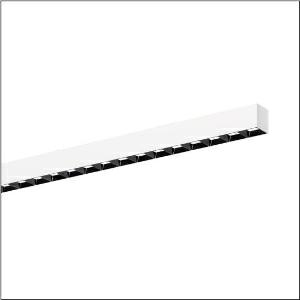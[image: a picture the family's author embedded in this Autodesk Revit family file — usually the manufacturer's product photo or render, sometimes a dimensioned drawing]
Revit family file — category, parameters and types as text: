
# Revit family: silica_r__21_51mx22dc4awb_3425
name_source: partatom
category: Lighting Fixtures
units: mm (PartAtom-declared; Revit-internal decimal feet)

## family parameters
Cut with Voids When Loaded = No
Host = Face
Light Source = No
Part Type = Normal
Room Calculation Point = No
Round Connector Dimension = Use Diameter
Shared = No

## types (1)
- --- (1 x LED, 10800 lm, 64.7 W, 4000K)
    Apparent Load = 65 VA
    CIE Flux Codes = 86 100 100 100 100
    Color Rendering = 80
    Color Temperature = 4000K
    Default Elevation = 1800 mm
    Description = Silica® 21, office luminaire, primary light control with darklight reflector, of PMMA, black, CAT 2 (L<= 3000cd/m²), light emission: direct distribution, primary light characteristic: symmetric, installation type: surface-mounted, LED, rated luminous flux: 10.800lm, luminous efficacy: 167lm/W, light colour: 840, colour temperature: 4000K, with terminal, 3+2-pole, max. 2.5mm², mains connection: 220..240V, AC, 50/60Hz, rated input power: 64.7W, luminaire housing, of aluminium, traffic white (RAL 9016), length: 3.004mm, width: 53mm, height: 53mm, protection rating (complete): IP20, insulation class (complete): insulation class I (protective earthing), certification: CE, permissible operating ambient temperature: 0..+35°C, standard: EN 50419, packaging unit: 1 piece
    Height = 0 mm  [stored 0 ft]
    Lamp = 1 x LED
    Lamp Light Flux = 10800 lm
    Lamp Power = 64.7 W
    Lamp count = 1
    Length = 3004 mm
    Luminous efficacy = 167 lm/W
    Manufacturer = Siteco
    ModVariant = No
    Model = 51MX22DC4AWB
    Mounting Place = Ceiling
    Mounting Type = Recessed
    Number of Poles = 1
    OnlyDefault = Yes
    Power Factor = 1
    Product Name = Silica® 21
    Product group = office luminaire | ceiling recessed
    ProductGroupID = 400
    Protection Class = Protection class I
    Protection Degree = IP 20
    RLX_Detail_Level = 1
    RLX_Emergency_Light_Flux = 0 lm
    RLX_Emergency_Type = 0
    RLX_Emergency_Type_DB = No
    RlxData = <blob elided: 61837 chars, md5=58495a07>
    Socket = socket
    Standby Power = 0 W
    System Light Flux = 10800 lm
    System Power = 65 W
    Type Comments = factory setting: luminous flux: 100 % | dim-lin: 254 | 366 mA
    Type Image = l_1335873.jpg
    URL = http://relux.com
    VarID = @adj_095141
    Voltage = 0 V
    Weight = 0.00 kg
    Width = 53 mm

note: [stored X ft] marks values corroborated as IEEE doubles in the binary element streams (Revit-internal decimal feet)

## geometry (parser evidence)
native form markers: Blend x4, Sweep x12
no freeform markers — native parametric forms only
